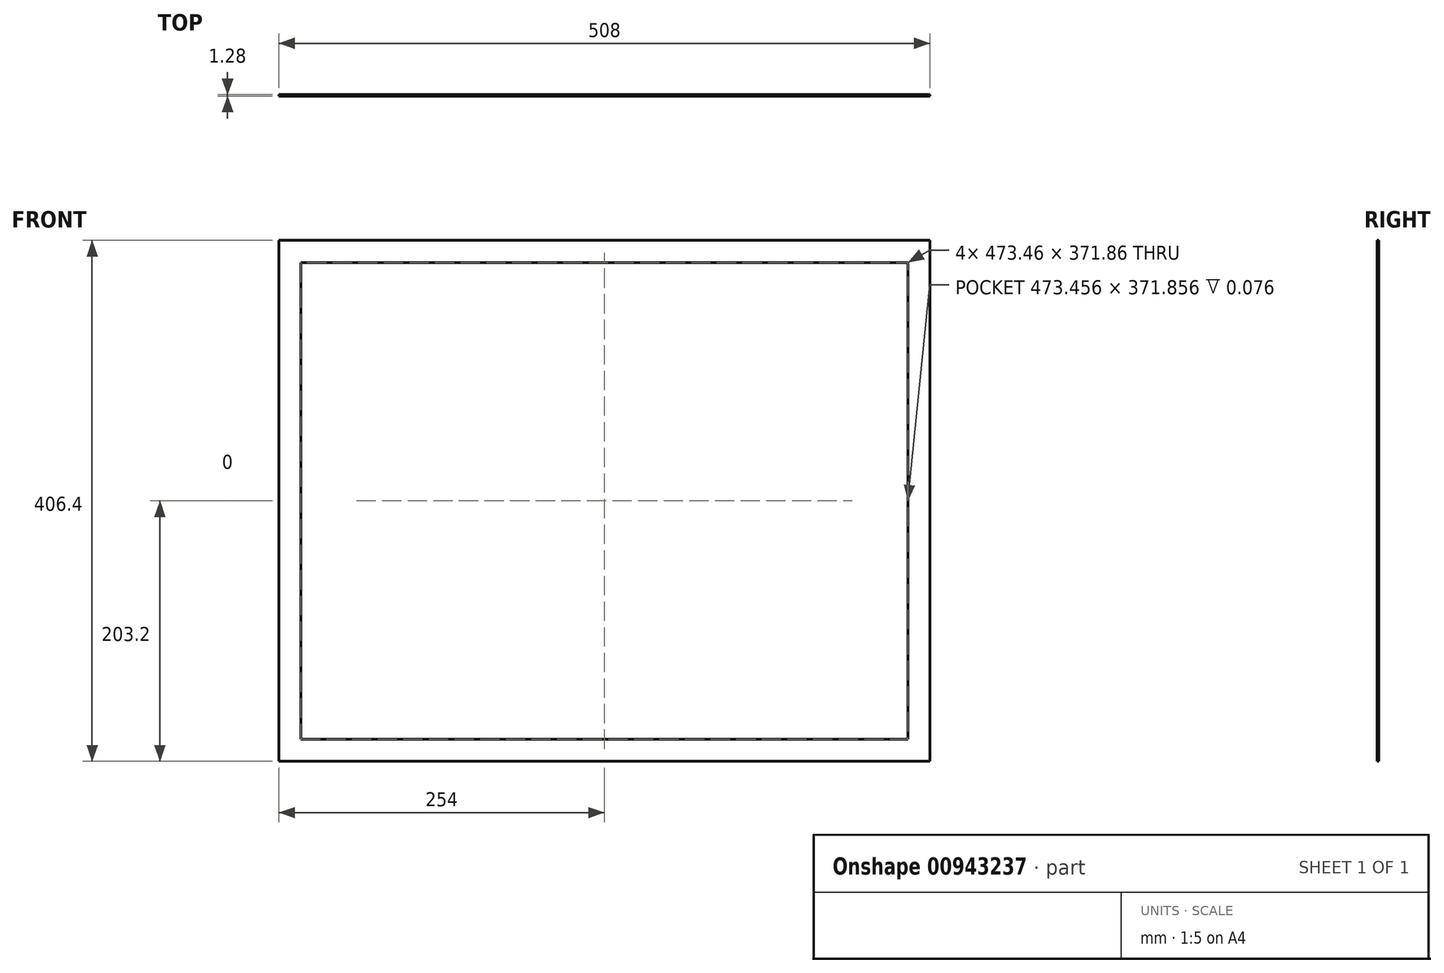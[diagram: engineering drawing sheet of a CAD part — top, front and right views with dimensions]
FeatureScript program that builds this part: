
annotation { "Feature Type Name" : "Feature", "Feature Type Description" : "" }
export const myFeature = defineFeature(function(context is Context, id is Id, definition is map)
    precondition{}
    {
        {
            var Q0;
            Q0=qCreatedBy(makeId("Front.planeOp"),FACE);
            var sketch = newSketch(context, id + "F0", { "sketchPlane" : qUnion([Q0])});
            skLineSegment(sketch, "E0.bottom", {"start": v(-254, 203.2) * mm, "end": v(254, 203.2) * mm});
            skLineSegment(sketch, "E0.top", {"start": v(-254, -203.2) * mm, "end": v(254, -203.2) * mm});
            skLineSegment(sketch, "E0.left", {"start": v(-254, 203.2) * mm, "end": v(-254, -203.2) * mm});
            skLineSegment(sketch, "E0.right", {"start": v(254, 203.2) * mm, "end": v(254, -203.2) * mm});
            skLineSegment(sketch, "E1", {"start": v(-254, -203.2) * mm, "end": v(254, 203.2) * mm, "construction": true});
            skLineSegment(sketch, "E2.bottom", {"start": v(-236.73, 185.93) * mm, "end": v(236.73, 185.93) * mm, "construction": true});
            skLineSegment(sketch, "E2.top", {"start": v(-236.73, -185.93) * mm, "end": v(236.73, -185.93) * mm, "construction": true});
            skLineSegment(sketch, "E2.left", {"start": v(-236.73, 185.93) * mm, "end": v(-236.73, -185.93) * mm, "construction": true});
            skLineSegment(sketch, "E2.right", {"start": v(236.73, 185.93) * mm, "end": v(236.73, -185.93) * mm, "construction": true});
            skSolve(sketch);
        }
        {
            var Q0;
            Q0 = qSketchRegion(id + "F0", true);
            extrude(context, id + "F1", {"entities" : qUnion([Q0]), "endBound" : BoundingType.SYMMETRIC, "depth" : 1.27 * mm, "offsetDistance" : 25.4 * mm});
        }
        {
            var Q0;
            Q0=makeQuery(id+"F1.opExtrude","CAP_FACE",FACE,{"disambiguationData":[OSD([sQuery(id+"F0.wireOp",EDGE,"E0.bottom"),sQuery(id+"F0.wireOp",EDGE,"E0.top"),sQuery(id+"F0.wireOp",EDGE,"E0.left"),sQuery(id+"F0.wireOp",EDGE,"E0.right")])],"isStart":false});
            var sketch = newSketch(context, id + "F2", { "sketchPlane" : qUnion([Q0])});
            skLineSegment(sketch, "E3.bottom", {"start": v(-236.73, 185.93) * mm, "end": v(236.73, 185.93) * mm});
            skLineSegment(sketch, "E3.top", {"start": v(-236.73, -185.93) * mm, "end": v(236.73, -185.93) * mm});
            skLineSegment(sketch, "E3.left", {"start": v(-236.73, 185.93) * mm, "end": v(-236.73, -185.93) * mm});
            skLineSegment(sketch, "E3.right", {"start": v(236.73, 185.93) * mm, "end": v(236.73, -185.93) * mm});
            skSolve(sketch);
        }
        {
            var Q0;
            Q0 = qSketchRegion(id + "F2", true);
            extrude(context, id + "F3", {"entities" : qUnion([Q0]), "operationType" : NewBodyOperationType.REMOVE, "oppositeDirection" : true, "depth" : 0.08 * mm, "offsetDistance" : 25.4 * mm});
        }
    });
